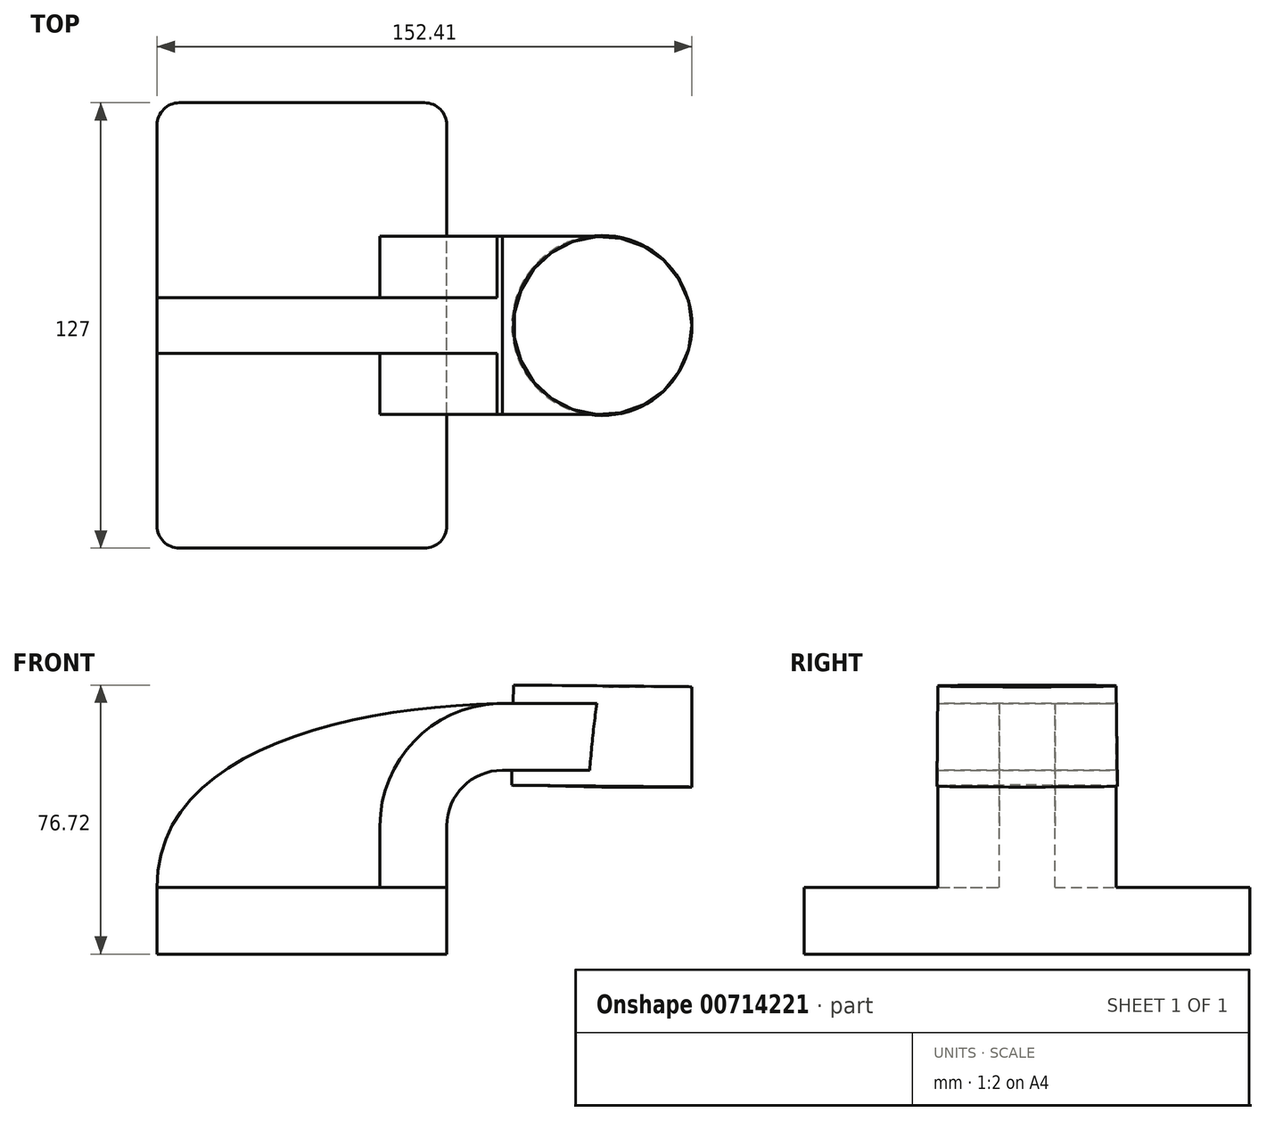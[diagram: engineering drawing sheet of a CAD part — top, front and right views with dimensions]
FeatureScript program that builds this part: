
annotation { "Feature Type Name" : "Feature", "Feature Type Description" : "" }
export const myFeature = defineFeature(function(context is Context, id is Id, definition is map)
    precondition{}
    {
        {
            var Q0;
            Q0=qCreatedBy(makeId("Front.planeOp"),FACE);
            var sketch = newSketch(context, id + "F0", { "sketchPlane" : qUnion([Q0])});
            skLineSegment(sketch, "E0.bottom", {"start": v(-41.28, -9.53) * mm, "end": v(41.28, -9.53) * mm});
            skLineSegment(sketch, "E0.top", {"start": v(-41.28, 9.53) * mm, "end": v(41.28, 9.53) * mm});
            skLineSegment(sketch, "E0.left", {"start": v(-41.28, -9.53) * mm, "end": v(-41.28, 9.53) * mm});
            skLineSegment(sketch, "E0.right", {"start": v(41.28, -9.53) * mm, "end": v(41.28, 9.53) * mm});
            skPoint(sketch, "E0.middle", {"position": v(0, 0) * mm});
            skLineSegment(sketch, "E1.bottom", {"start": v(60.32, 38.1) * mm, "end": v(111.12, 38.1) * mm});
            skLineSegment(sketch, "E1.top", {"start": v(60.32, 66.67) * mm, "end": v(111.12, 66.67) * mm});
            skLineSegment(sketch, "E1.left", {"start": v(60.32, 38.1) * mm, "end": v(60.32, 66.67) * mm});
            skLineSegment(sketch, "E1.right", {"start": v(111.12, 38.1) * mm, "end": v(111.12, 66.67) * mm});
            skPoint(sketch, "E1.middle", {"position": v(85.72, 52.39) * mm});
            skLineSegment(sketch, "E2", {"start": v(41.27, 9.53) * mm, "end": v(41.27, 27) * mm});
            skArc(sketch, "E3", {"start": v(41.27, 27) * mm, "mid": v(45.92, 38.23) * mm, "end": v(57.15, 42.88) * mm});
            skLineSegment(sketch, "E4.0", {"start": v(57.15, 61.93) * mm, "end": v(85.75, 61.93) * mm});
            skArc(sketch, "E4.1", {"start": v(22.23, 27) * mm, "mid": v(32.45, 51.7) * mm, "end": v(57.15, 61.93) * mm});
            skLineSegment(sketch, "E4.2", {"start": v(22.22, 9.53) * mm, "end": v(22.22, 27) * mm});
            skLineSegment(sketch, "E5", {"start": v(85.72, 66.67) * mm, "end": v(85.44, 38.1) * mm});
            skFitSpline(sketch, "E6", {"points": [v(-41.28, 9.53) * mm, v(57.15, 61.93) * mm], "startDerivative": vector(-0.75, 115.57) * mm, "endDerivative": vector(134.7, 2.5) * mm});
            skLineSegment(sketch, "E7", {"start": v(57.15, 42.88) * mm, "end": v(85.48, 42.88) * mm});
            skSolve(sketch);
        }
        {
            var Q0;
            Q0=makeQuery(id+"F0.imprint","IMPRINT",FACE,{"disambiguationData":[TD([[makeQuery(id+"F0.imprint","IMPRINT",EDGE,{"derivedFrom":sQuery(id+"F0.wireOp",EDGE,"E0.bottom")}),1.0]])]});
            extrude(context, id + "F1", {"entities" : qUnion([Q0]), "endBound" : BoundingType.SYMMETRIC, "depth" : 127 * mm, "offsetDistance" : 25.4 * mm});
        }
        {
            var Q0;
            {var subQ0=sQuery(id+"F0.wireOp",EDGE,"E7");var subQ1=sQuery(id+"F0.wireOp",EDGE,"E1.left");var subQ2=makeQuery(id+"F0.imprint","INTERSECT",VERTEX,{"derivedFrom":[subQ1,subQ0]});Q0=makeQuery(id+"F0.imprint","IMPRINT",FACE,{"disambiguationData":[TD([[makeQuery(id+"F0.imprint","IMPRINT",EDGE,{"disambiguationData":[TD([[subQ2,-1.0]])],"derivedFrom":subQ1}),-1.0]])]});}
            var Q1;
            {var subQ4=sQuery(id+"F0.wireOp",EDGE,"E2");Q1=makeQuery(id+"F0.imprint","IMPRINT",FACE,{"disambiguationData":[TD([[makeQuery(id+"F0.imprint","IMPRINT",EDGE,{"derivedFrom":subQ4}),1.0]])]});}
            extrude(context, id + "F2", {"entities" : qUnion([Q0, Q1]), "operationType" : NewBodyOperationType.ADD, "endBound" : BoundingType.SYMMETRIC, "depth" : 50.8 * mm, "offsetDistance" : 25.4 * mm});
        }
        {
            var Q0;
            {var subQ3=sQuery(id+"F0.wireOp",EDGE,"E4.2");Q0=makeQuery(id+"F0.imprint","IMPRINT",FACE,{"disambiguationData":[TD([[makeQuery(id+"F0.imprint","IMPRINT",EDGE,{"derivedFrom":subQ3}),1.0]])]});}
            extrude(context, id + "F3", {"entities" : qUnion([Q0]), "operationType" : NewBodyOperationType.ADD, "endBound" : BoundingType.SYMMETRIC, "depth" : 15.88 * mm, "offsetDistance" : 25.4 * mm});
        }
        {
            var Q0;
            {var subQ4=sQuery(id+"F0.wireOp",EDGE,"E1.right");Q0=makeQuery(id+"F0.imprint","IMPRINT",FACE,{"disambiguationData":[TD([[makeQuery(id+"F0.imprint","IMPRINT",EDGE,{"derivedFrom":subQ4}),1.0]])]});}
            var Q1;
            Q1=sQuery(id+"F0.wireOp",EDGE,"E5");
            revolve(context, id + "F4", {"operationType" : NewBodyOperationType.ADD, "surfaceOperationType" : NewSurfaceOperationType.NEW, "entities" : qUnion([Q0]), "axis" : qUnion([Q1]), "revolveType" : RevolveType.FULL});
        }
        {
            var Q0;
            Q0=makeQuery(id+"F1.opExtrude","CAP_EDGE",EDGE,{"disambiguationData":[OSD([sQuery(id+"F0.wireOp",EDGE,"E0.left")])],"isStart":false});
            var Q1;
            Q1=makeQuery(id+"F1.opExtrude","CAP_EDGE",EDGE,{"disambiguationData":[OSD([sQuery(id+"F0.wireOp",EDGE,"E0.right")])],"isStart":false});
            var Q2;
            Q2=makeQuery(id+"F1.opExtrude","CAP_EDGE",EDGE,{"disambiguationData":[OSD([sQuery(id+"F0.wireOp",EDGE,"E0.right")])],"isStart":true});
            var Q3;
            Q3=makeQuery(id+"F1.opExtrude","CAP_EDGE",EDGE,{"disambiguationData":[OSD([sQuery(id+"F0.wireOp",EDGE,"E0.left")])],"isStart":true});
            fillet(context, id + "F5", {"entities" : qUnion([Q0, Q1, Q2, Q3]), "radius" : 6.35 * mm, "tangentPropagation" : true, "allowEdgeOverflow" : false});
        }
    });
